# Revit family: Worksurface-Teknion-EMTW_Navigate_Height_Adjustable_Emote_With-Base-R2016
name_source: partatom
category: Furniture
revit_build: Autodesk Revit 2018 (Build: 20190510_1515(x64)
units: mm (PartAtom-declared; Revit-internal decimal feet)

## family parameters
Always vertical = Yes
Cut with Voids When Loaded = No
OmniClass Number = 23.40.20.00
OmniClass Title = General Furniture and Specialties
Room Calculation Point = No
Shared = Yes
Work Plane-Based = No

## types (4) — shared parameters
Assembly Code = E2020200
Manufacturer = Teknion
Manufacturer Fax = 416.661.4586
Part Number = EMTW
Product Documentation Link = https://assets.teknion.com
Product Line = Emote
Product Page URL = https://www.teknion.com
Series = Emote
Sustainability Data = https://www.teknion.com
URL = www.teknion.com
Unit Weight URL = http://www.teknion.com
Warranty = http://www.teknion.com

## per-type parameters (varying)
| type | Description | Model | Round Corner | Square Corner |
| Rectangular Top, Square Edge | Worksurface for Navigate Extended Range HA Table with Base, Extended Electric Emote Base Mechanics, Rectangular Top Square Edge, 30" Depth | EMTW9MR30__ | No | Yes |
| Eased Corners, Square Edge | Worksurface for Navigate Extended Range HA Table with Base, Extended Electric Emote Base Mechanics, Eased Corners Square Edge, 30" Depth | EMTW9ME30__ | Yes | No |
| Rectangular Top, Knife Edge | Worksurface for Navigate Extended Range HA Table with Base, Extended Electric Emote Base Mechanics, Rectangular Top Knife Edge, 30" Depth | EMTW9MK30__ | No | Yes |
| Eased Corner, Knife Edge | Worksurface for Navigate Extended Range HA Table with Base, Extended Electric Emote Base Mechanics, Rectangular Top Square Edge, 30" Depth | EMTW9MR30__ | Yes | No |

## geometry (parser evidence)
native form markers: Blend x49, Sweep x2
no freeform markers — native parametric forms only
